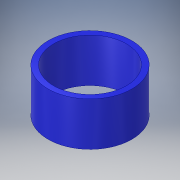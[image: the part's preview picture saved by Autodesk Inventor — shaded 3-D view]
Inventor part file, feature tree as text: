
AUTODESK INVENTOR PART (.ipt)
format: ipt  version: 2018 (Build 220112000, 112)  size: 116,736 bytes
history: native  units: in
note: dims shown in document units (in); Inventor stores cm internally (conversion verified against a paired STEP export)
features: revolve x1, sketch x1
ambient origin geometry x8: Origin, YZ Plane, XZ Plane, XY Plane, X Axis, Y Axis, Z Axis, Center Point
bodies: Solid1 (feature_tree)
feature tree (2):
  revolve  "Revolution1"  [1 undecoded]
  sketch  "Sketch1"  dims[d0=1.5625in d1=5.0in d3=14.0in d4=90.0deg d5=1.4375in d6=1.5in d7=2.5in d9=0.75in d10=0.25in d11=0.75in d12=0.1875in]
note: 1 required parameter value undecoded (feature->parameter linkage not recoverable at this tier; creation-order binding heuristic only, values carry confidence <= 0.55)
